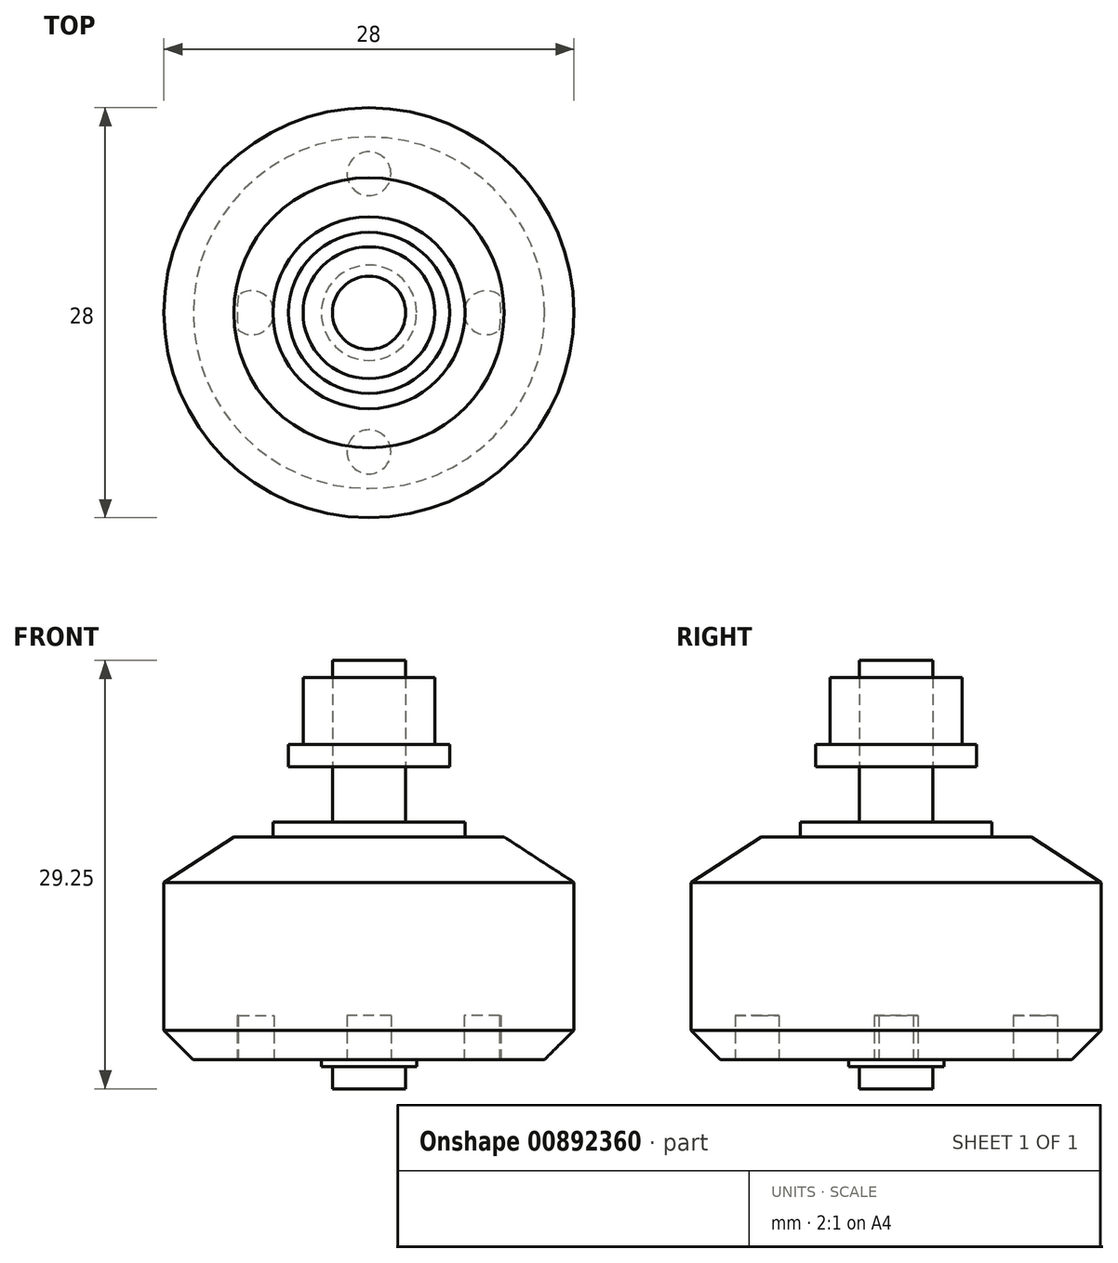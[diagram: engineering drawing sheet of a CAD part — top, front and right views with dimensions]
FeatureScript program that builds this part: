
annotation { "Feature Type Name" : "Feature", "Feature Type Description" : "" }
export const myFeature = defineFeature(function(context is Context, id is Id, definition is map)
    precondition{}
    {
        {
            var Q0;
            Q0=qCreatedBy(makeId("Top.planeOp"),FACE);
            var sketch = newSketch(context, id + "F0", { "sketchPlane" : qUnion([Q0])});
            skCircle(sketch, "E0", {"center": v(0, 0) * mm, "radius": 14 * mm});
            skCircle(sketch, "E1", {"center": v(0, 0) * mm, "radius": 6.55 * mm});
            skCircle(sketch, "E2", {"center": v(0, 0) * mm, "radius": 2.5 * mm});
            skLineSegment(sketch, "E3", {"start": v(-29.61, 0) * mm, "end": v(25.95, 0) * mm, "construction": true});
            skCircle(sketch, "E4", {"center": v(-8, 0) * mm, "radius": 1.5 * mm});
            skCircle(sketch, "E5", {"center": v(8, 0) * mm, "radius": 1.5 * mm});
            skCircle(sketch, "E6", {"center": v(0, -9.5) * mm, "radius": 1.5 * mm});
            skCircle(sketch, "E7", {"center": v(0, 9.5) * mm, "radius": 1.5 * mm});
            skCircle(sketch, "E8", {"center": v(0, 0) * mm, "radius": 9 * mm});
            skCircle(sketch, "E9", {"center": v(0, 0) * mm, "radius": 3.25 * mm});
            skSolve(sketch);
        }
        {
            var Q0;
            Q0=makeQuery(id+"F0.imprint","IMPRINT",FACE,{"disambiguationData":[TD([[makeQuery(id+"F0.imprint","IMPRINT",EDGE,{"derivedFrom":sQuery(id+"F0.wireOp",EDGE,"E0")}),1.0]])]});
            var Q1;
            {var subQ0=sQuery(id+"F0.wireOp",EDGE,"E4");var subQ1=sQuery(id+"F0.wireOp",EDGE,"E1");var subQ2=makeQuery(id+"F0.imprint","INTERSECT",VERTEX,{"disambiguationData":[OD(0.0)],"derivedFrom":[subQ1,subQ0]});Q1=makeQuery(id+"F0.imprint","IMPRINT",FACE,{"disambiguationData":[TD([[makeQuery(id+"F0.imprint","IMPRINT",EDGE,{"disambiguationData":[TD([[subQ2,-1.0]])],"derivedFrom":subQ1}),-1.0]])]});}
            var Q2;
            {var subQ0=sQuery(id+"F0.wireOp",EDGE,"E5");var subQ1=sQuery(id+"F0.wireOp",EDGE,"E1");var subQ2=makeQuery(id+"F0.imprint","INTERSECT",VERTEX,{"disambiguationData":[OD(0.0)],"derivedFrom":[subQ1,subQ0]});Q2=makeQuery(id+"F0.imprint","IMPRINT",FACE,{"disambiguationData":[TD([[makeQuery(id+"F0.imprint","IMPRINT",EDGE,{"disambiguationData":[TD([[subQ2,1.0]])],"derivedFrom":subQ1}),-1.0]])]});}
            var Q3;
            Q3=makeQuery(id+"F0.imprint","IMPRINT",FACE,{"disambiguationData":[TD([[makeQuery(id+"F0.imprint","IMPRINT",EDGE,{"derivedFrom":sQuery(id+"F0.wireOp",EDGE,"E6")}),1.0]])]});
            var Q4;
            Q4=makeQuery(id+"F0.imprint","IMPRINT",FACE,{"disambiguationData":[TD([[makeQuery(id+"F0.imprint","IMPRINT",EDGE,{"derivedFrom":sQuery(id+"F0.wireOp",EDGE,"E7")}),1.0]])]});
            var Q5;
            {var subQ0=sQuery(id+"F0.wireOp",EDGE,"E8");var subQ1=sQuery(id+"F0.wireOp",EDGE,"E4");var subQ2=makeQuery(id+"F0.imprint","INTERSECT",VERTEX,{"disambiguationData":[OD(0.0)],"derivedFrom":[subQ1,subQ0]});Q5=makeQuery(id+"F0.imprint","IMPRINT",FACE,{"disambiguationData":[TD([[makeQuery(id+"F0.imprint","IMPRINT",EDGE,{"disambiguationData":[TD([[subQ2,-1.0]])],"derivedFrom":subQ1}),1.0]])]});}
            var Q6;
            {var subQ0=sQuery(id+"F0.wireOp",EDGE,"E8");var subQ1=sQuery(id+"F0.wireOp",EDGE,"E5");var subQ2=makeQuery(id+"F0.imprint","INTERSECT",VERTEX,{"disambiguationData":[OD(0.0)],"derivedFrom":[subQ1,subQ0]});Q6=makeQuery(id+"F0.imprint","IMPRINT",FACE,{"disambiguationData":[TD([[makeQuery(id+"F0.imprint","IMPRINT",EDGE,{"disambiguationData":[TD([[subQ2,1.0]])],"derivedFrom":subQ1}),1.0]])]});}
            var Q7;
            {var subQ1=sQuery(id+"F0.wireOp",EDGE,"E1");var subQ8=sQuery(id+"F0.wireOp",EDGE,"E4");var subQ9=makeQuery(id+"F0.imprint","INTERSECT",VERTEX,{"disambiguationData":[OD(0.0)],"derivedFrom":[subQ1,subQ8]});Q7=makeQuery(id+"F0.imprint","IMPRINT",FACE,{"disambiguationData":[TD([[makeQuery(id+"F0.imprint","IMPRINT",EDGE,{"disambiguationData":[TD([[subQ9,1.0]])],"derivedFrom":subQ1}),-1.0]])]});}
            var Q8;
            {var subQ4=sQuery(id+"F0.wireOp",EDGE,"E4");var subQ5=sQuery(id+"F0.wireOp",EDGE,"E1");var subQ6=makeQuery(id+"F0.imprint","INTERSECT",VERTEX,{"disambiguationData":[OD(1.0)],"derivedFrom":[subQ5,subQ4]});Q8=makeQuery(id+"F0.imprint","IMPRINT",FACE,{"disambiguationData":[TD([[makeQuery(id+"F0.imprint","IMPRINT",EDGE,{"disambiguationData":[TD([[subQ6,-1.0]])],"derivedFrom":subQ5}),-1.0]])]});}
            var Q9;
            Q9=makeQuery(id+"F0.imprint","IMPRINT",FACE,{"disambiguationData":[TD([[makeQuery(id+"F0.imprint","IMPRINT",EDGE,{"derivedFrom":sQuery(id+"F0.wireOp",EDGE,"E2")}),-1.0]])]});
            var Q10;
            Q10=makeQuery(id+"F0.imprint","IMPRINT",FACE,{"disambiguationData":[TD([[makeQuery(id+"F0.imprint","IMPRINT",EDGE,{"derivedFrom":sQuery(id+"F0.wireOp",EDGE,"E2")}),1.0]])]});
            extrude(context, id + "F1", {"entities" : qUnion([Q0, Q1, Q2, Q3, Q4, Q5, Q6, Q7, Q8, Q9, Q10]), "depth" : 15.2 * mm, "offsetDistance" : 25 * mm});
        }
        {
            var Q0;
            Q0=makeQuery(id+"F0.imprint","IMPRINT",FACE,{"disambiguationData":[TD([[makeQuery(id+"F0.imprint","IMPRINT",EDGE,{"derivedFrom":sQuery(id+"F0.wireOp",EDGE,"E1")}),1.0]])]});
            var Q1;
            {var subQ0=sQuery(id+"F0.wireOp",EDGE,"E4");var subQ1=sQuery(id+"F0.wireOp",EDGE,"E1");var subQ2=makeQuery(id+"F0.imprint","INTERSECT",VERTEX,{"disambiguationData":[OD(0.0)],"derivedFrom":[subQ1,subQ0]});Q1=makeQuery(id+"F0.imprint","IMPRINT",FACE,{"disambiguationData":[TD([[makeQuery(id+"F0.imprint","IMPRINT",EDGE,{"disambiguationData":[TD([[subQ2,-1.0]])],"derivedFrom":subQ1}),1.0]])]});}
            var Q2;
            {var subQ0=sQuery(id+"F0.wireOp",EDGE,"E5");var subQ1=sQuery(id+"F0.wireOp",EDGE,"E1");var subQ2=makeQuery(id+"F0.imprint","INTERSECT",VERTEX,{"disambiguationData":[OD(0.0)],"derivedFrom":[subQ1,subQ0]});Q2=makeQuery(id+"F0.imprint","IMPRINT",FACE,{"disambiguationData":[TD([[makeQuery(id+"F0.imprint","IMPRINT",EDGE,{"disambiguationData":[TD([[subQ2,1.0]])],"derivedFrom":subQ1}),1.0]])]});}
            var Q3;
            Q3=makeQuery(id+"F0.imprint","IMPRINT",FACE,{"disambiguationData":[TD([[makeQuery(id+"F0.imprint","IMPRINT",EDGE,{"derivedFrom":sQuery(id+"F0.wireOp",EDGE,"E2")}),-1.0]])]});
            extrude(context, id + "F2", {"entities" : qUnion([Q0, Q1, Q2, Q3]), "operationType" : NewBodyOperationType.ADD, "depth" : 16.2 * mm, "offsetDistance" : 25 * mm});
        }
        {
            var Q0;
            Q0=makeQuery(id+"F0.imprint","IMPRINT",FACE,{"disambiguationData":[TD([[makeQuery(id+"F0.imprint","IMPRINT",EDGE,{"derivedFrom":sQuery(id+"F0.wireOp",EDGE,"E2")}),1.0]])]});
            extrude(context, id + "F3", {"entities" : qUnion([Q0]), "operationType" : NewBodyOperationType.ADD, "depth" : 27.25 * mm, "offsetDistance" : 25 * mm, "hasSecondDirection" : true, "secondDirectionOppositeDirection" : true, "secondDirectionDepth" : 2 * mm});
        }
        {
            var Q0;
            Q0=makeQuery(id+"F0.imprint","IMPRINT",FACE,{"disambiguationData":[TD([[makeQuery(id+"F0.imprint","IMPRINT",EDGE,{"derivedFrom":sQuery(id+"F0.wireOp",EDGE,"E2")}),-1.0]])]});
            extrude(context, id + "F4", {"entities" : qUnion([Q0]), "operationType" : NewBodyOperationType.ADD, "oppositeDirection" : true, "depth" : 0.5 * mm, "offsetDistance" : 25 * mm});
        }
        {
            var Q0;
            Q0=makeQuery(id+"F1.opExtrude","CAP_EDGE",EDGE,{"disambiguationData":[OSD([sQuery(id+"F0.wireOp",EDGE,"E0")])],"isStart":false});
            chamfer(context, id + "F5", {"entities" : qUnion([Q0]), "chamferType" : ChamferType.OFFSET_ANGLE, "width" : 3.1 * mm, "oppositeDirection" : true, "angle" : 57 * degree, "tangentPropagation" : true});
        }
        {
            var Q0;
            Q0=makeQuery(id+"F1.opExtrude","CAP_EDGE",EDGE,{"disambiguationData":[OSD([sQuery(id+"F0.wireOp",EDGE,"E0")])],"isStart":true});
            chamfer(context, id + "F6", {"entities" : qUnion([Q0]), "chamferType" : ChamferType.OFFSET_ANGLE, "width" : 2 * mm, "oppositeDirection" : false, "angle" : 45 * degree, "tangentPropagation" : true});
        }
        {
            var Q0;
            Q0=qCreatedBy(makeId("Front.planeOp"),FACE);
            var sketch = newSketch(context, id + "F7", { "sketchPlane" : qUnion([Q0])});
            skLineSegment(sketch, "E10", {"start": v(2.5, 20) * mm, "end": v(5.5, 20) * mm});
            skLineSegment(sketch, "E11", {"start": v(5.5, 20) * mm, "end": v(5.5, 21.5) * mm});
            skLineSegment(sketch, "E12", {"start": v(5.5, 21.5) * mm, "end": v(4.5, 21.5) * mm});
            skLineSegment(sketch, "E13", {"start": v(2.5, 20) * mm, "end": v(2.5, 26.1) * mm});
            skLineSegment(sketch, "E14", {"start": v(0, 0) * mm, "end": v(0, 48.2) * mm, "construction": true});
            skLineSegment(sketch, "E15", {"start": v(4.5, 21.5) * mm, "end": v(4.5, 26.1) * mm});
            skLineSegment(sketch, "E16", {"start": v(2.5, 26.1) * mm, "end": v(4.5, 26.1) * mm});
            skSolve(sketch);
        }
        {
            var Q0;
            Q0=qSketchRegion(id+"F7",true);
            var Q1;
            Q1=sQuery(id+"F7.wireOp",EDGE,"E14");
            revolve(context, id + "F8", {"surfaceOperationType" : NewSurfaceOperationType.NEW, "entities" : qUnion([Q0]), "axis" : qUnion([Q1]), "revolveType" : RevolveType.FULL});
        }
        {
            var Q0;
            {var subQ0=sQuery(id+"F0.wireOp",EDGE,"E4");var subQ1=sQuery(id+"F0.wireOp",EDGE,"E1");var subQ2=makeQuery(id+"F0.imprint","INTERSECT",VERTEX,{"disambiguationData":[OD(0.0)],"derivedFrom":[subQ1,subQ0]});Q0=makeQuery(id+"F0.imprint","IMPRINT",FACE,{"disambiguationData":[TD([[makeQuery(id+"F0.imprint","IMPRINT",EDGE,{"disambiguationData":[TD([[subQ2,-1.0]])],"derivedFrom":subQ1}),1.0]])]});}
            var Q1;
            {var subQ0=sQuery(id+"F0.wireOp",EDGE,"E4");var subQ1=sQuery(id+"F0.wireOp",EDGE,"E1");var subQ2=makeQuery(id+"F0.imprint","INTERSECT",VERTEX,{"disambiguationData":[OD(0.0)],"derivedFrom":[subQ1,subQ0]});Q1=makeQuery(id+"F0.imprint","IMPRINT",FACE,{"disambiguationData":[TD([[makeQuery(id+"F0.imprint","IMPRINT",EDGE,{"disambiguationData":[TD([[subQ2,-1.0]])],"derivedFrom":subQ1}),-1.0]])]});}
            var Q2;
            Q2=makeQuery(id+"F0.imprint","IMPRINT",FACE,{"disambiguationData":[TD([[makeQuery(id+"F0.imprint","IMPRINT",EDGE,{"derivedFrom":sQuery(id+"F0.wireOp",EDGE,"E6")}),1.0]])]});
            var Q3;
            {var subQ0=sQuery(id+"F0.wireOp",EDGE,"E5");var subQ1=sQuery(id+"F0.wireOp",EDGE,"E1");var subQ2=makeQuery(id+"F0.imprint","INTERSECT",VERTEX,{"disambiguationData":[OD(0.0)],"derivedFrom":[subQ1,subQ0]});Q3=makeQuery(id+"F0.imprint","IMPRINT",FACE,{"disambiguationData":[TD([[makeQuery(id+"F0.imprint","IMPRINT",EDGE,{"disambiguationData":[TD([[subQ2,1.0]])],"derivedFrom":subQ1}),-1.0]])]});}
            var Q4;
            {var subQ0=sQuery(id+"F0.wireOp",EDGE,"E5");var subQ1=sQuery(id+"F0.wireOp",EDGE,"E1");var subQ2=makeQuery(id+"F0.imprint","INTERSECT",VERTEX,{"disambiguationData":[OD(0.0)],"derivedFrom":[subQ1,subQ0]});Q4=makeQuery(id+"F0.imprint","IMPRINT",FACE,{"disambiguationData":[TD([[makeQuery(id+"F0.imprint","IMPRINT",EDGE,{"disambiguationData":[TD([[subQ2,1.0]])],"derivedFrom":subQ1}),1.0]])]});}
            var Q5;
            Q5=makeQuery(id+"F0.imprint","IMPRINT",FACE,{"disambiguationData":[TD([[makeQuery(id+"F0.imprint","IMPRINT",EDGE,{"derivedFrom":sQuery(id+"F0.wireOp",EDGE,"E7")}),1.0]])]});
            extrude(context, id + "F9", {"entities" : qUnion([Q0, Q1, Q2, Q3, Q4, Q5]), "operationType" : NewBodyOperationType.REMOVE, "depth" : 3 * mm, "offsetDistance" : 25 * mm});
        }
    });
